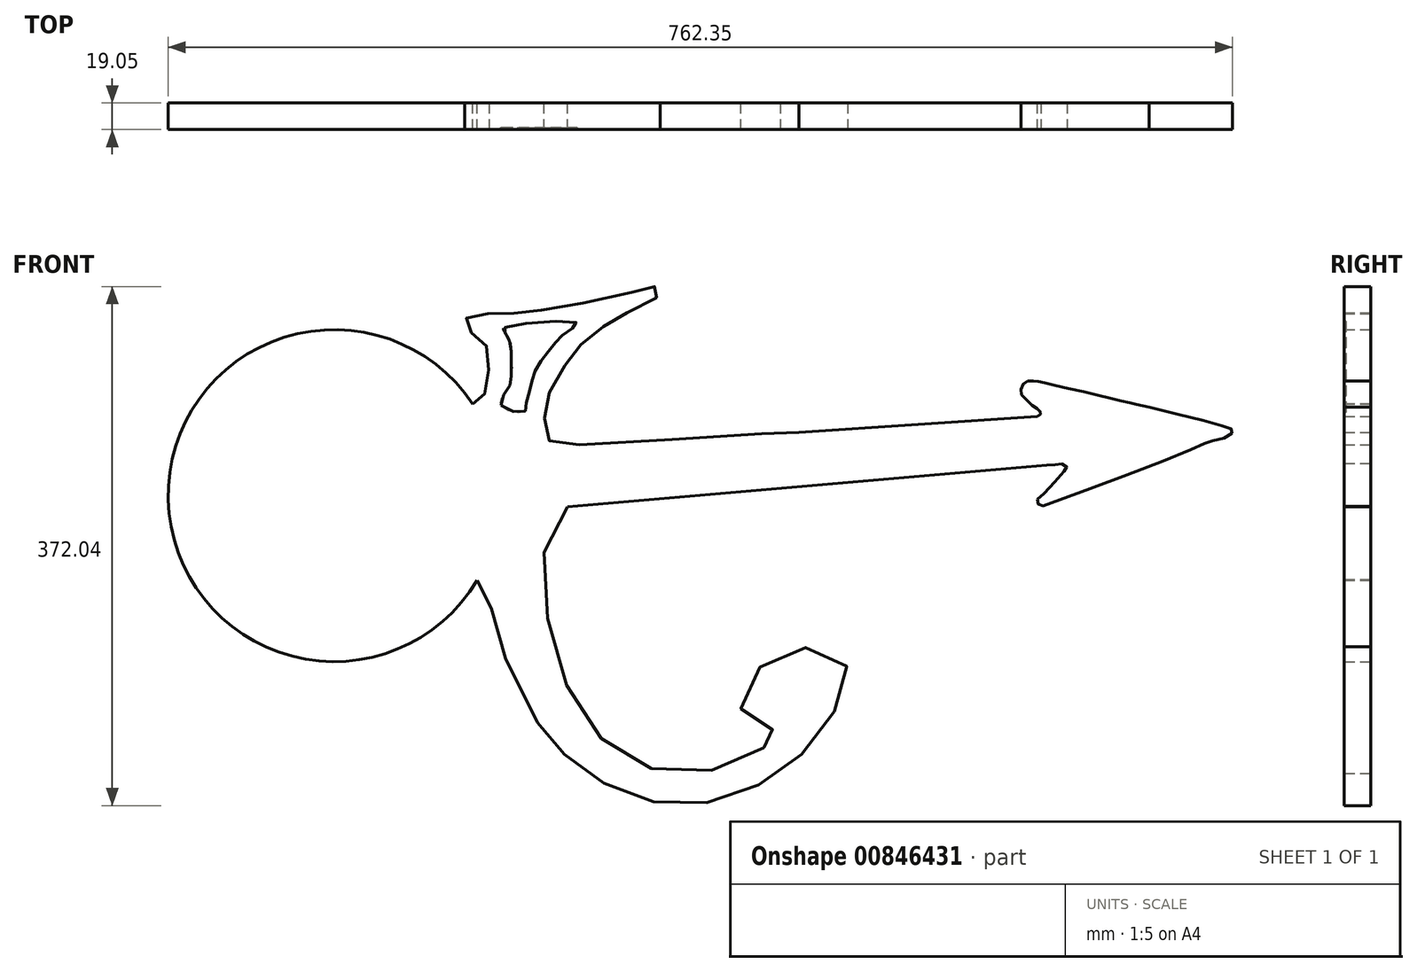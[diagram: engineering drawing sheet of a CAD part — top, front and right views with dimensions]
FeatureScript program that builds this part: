
annotation { "Feature Type Name" : "Feature", "Feature Type Description" : "" }
export const myFeature = defineFeature(function(context is Context, id is Id, definition is map)
    precondition{}
    {
        {
            var Q0;
            Q0=qCreatedBy(makeId("Front.planeOp"),FACE);
            var sketch = newSketch(context, id + "F0", { "sketchPlane" : qUnion([Q0])});
            skArc(sketch, "E0", {"start": v(-130.11, 85.53) * mm, "mid": v(-348.27, 16.89) * mm, "end": v(-127, -40.95) * mm});
            skFitSpline(sketch, "E1", {"points": [v(-130.11, 85.53) * mm, v(-127.54, 85.53) * mm, v(-123.05, 90.04) * mm, v(-119.7, 99.57) * mm, v(-118.57, 112.46) * mm, v(-119.41, 124.5) * mm, v(-123.05, 131.23) * mm, v(-130.11, 136) * mm, v(-134.82, 139.36) * mm, v(-135.38, 145.53) * mm, v(-130.11, 150) * mm, v(-118.29, 150.29) * mm, v(-104.56, 150.29) * mm, v(-90.55, 151.7) * mm, v(-71.5, 153.93) * mm, v(-25.54, 163.46) * mm, v(-2.84, 169.06) * mm, v(0, 169.62) * mm, v(3.6, 167.38) * mm, v(3.6, 164.02) * mm, v(-4.8, 158.14) * mm, v(-27.78, 146.93) * mm, v(-36.47, 141.04) * mm, v(-50.2, 130.4) * mm, v(-58.04, 121.15) * mm, v(-68.13, 107.42) * mm, v(-75.98, 91.16) * mm, v(-78.22, 78.55) * mm, v(-78.78, 65.95) * mm, v(-74.3, 58.1) * mm, v(-68.13, 56.14) * mm, v(74.22, 63.98) * mm, v(103.36, 65.1) * mm], "startDerivative": vector(181.45, -37.87) * mm, "endDerivative": vector(410.65, 5.44) * mm});
            skLineSegment(sketch, "E2", {"start": v(-62.29, 11.73) * mm, "end": v(280.92, 41.5) * mm});
            skLineSegment(sketch, "E3", {"start": v(103.36, 65.1) * mm, "end": v(274.42, 76.69) * mm});
            skFitSpline(sketch, "E4", {"points": [v(274.42, 76.69) * mm, v(276.7, 78.48) * mm, v(275.97, 80.66) * mm, v(270.52, 84.66) * mm, v(265.43, 89.75) * mm, v(262.7, 93.2) * mm, v(264.7, 100.47) * mm, v(271.25, 102.1) * mm, v(279.6, 100.65) * mm, v(323.94, 90.3) * mm, v(344.65, 85.39) * mm, v(354.18, 83.22) * mm], "startDerivative": vector(58.3, 31.52) * mm, "endDerivative": vector(96.9, -21.74) * mm});
            skFitSpline(sketch, "E5", {"points": [v(354.18, 83.22) * mm, v(411.37, 68.6) * mm, v(413.97, 66.88) * mm, v(412.24, 62.99) * mm, v(399.27, 59.1) * mm, v(388.04, 54.34) * mm, v(280.87, 13.29) * mm, v(275.68, 12.86) * mm, v(273.95, 16.31) * mm, v(277.4, 19.77) * mm, v(293.4, 37.06) * mm, v(295.56, 40.08) * mm, v(292.97, 42.24) * mm, v(288.65, 42.24) * mm, v(280.92, 41.5) * mm], "startDerivative": vector(481.46, -118.1) * mm, "endDerivative": vector(-146.74, -12.07) * mm});
            skFitSpline(sketch, "E6", {"points": [v(-127, -40.95) * mm, v(-121.29, -40.95) * mm, v(-118.6, -54.12) * mm, v(-113.25, -70.88) * mm, v(-106.54, -97.02) * mm, v(-86.43, -138.58) * mm, v(-75.7, -154.67) * mm, v(-66.32, -164.05) * mm, v(-51.58, -176.12) * mm, v(-32.8, -188.18) * mm, v(-11.36, -196.9) * mm, v(15.46, -202.26) * mm, v(38.25, -200.25) * mm, v(61.04, -193.54) * mm, v(87.85, -180.14) * mm, v(104.6, -166.73) * mm, v(121.37, -145.95) * mm, v(133.43, -127.18) * mm, v(138.8, -108.41) * mm, v(130.75, -92.33) * mm, v(109.3, -88.97) * mm, v(89.2, -94.34) * mm, v(70.42, -108.41) * mm, v(62.38, -126.51) * mm, v(63.72, -137.9) * mm, v(77.13, -146.62) * mm, v(87.85, -148.63) * mm, v(90.53, -151.31) * mm, v(85.17, -156.68) * mm, v(64.39, -168.07) * mm, v(36.9, -178.13) * mm, v(4.73, -177.46) * mm, v(-22.08, -166.73) * mm, v(-45.54, -145.95) * mm, v(-63.64, -114.45) * mm, v(-75.7, -73.56) * mm, v(-78.39, -40.95) * mm, v(-75.7, 0) * mm, v(-62.29, 11.73) * mm], "startDerivative": vector(493.19, 133.64) * mm, "endDerivative": vector(663.86, 344.27) * mm});
            skFitSpline(sketch, "E7", {"points": [v(-109.9, 84.64) * mm, v(-93.14, 79.95) * mm, v(-91.8, 85.3) * mm, v(-88.44, 98.05) * mm, v(-85.76, 108.77) * mm, v(-78.39, 120.17) * mm, v(-70.34, 130.22) * mm, v(-62.3, 137.6) * mm, v(-55.6, 143.63) * mm, v(-107.21, 140.28) * mm, v(-107.88, 138.26) * mm, v(-103.86, 130.9) * mm, v(-102.52, 118.83) * mm, v(-102.52, 104.08) * mm, v(-105.2, 96.03) * mm, v(-109.9, 84.64) * mm]});
            skSolve(sketch);
        }
        {
            var Q0;
            Q0=makeQuery(id+"F0.imprint","IMPRINT",FACE,{"disambiguationData":[TD([[makeQuery(id+"F0.imprint","IMPRINT",EDGE,{"derivedFrom":sQuery(id+"F0.wireOp",EDGE,"E0")}),1.0]])]});
            extrude(context, id + "F1", {"entities" : qUnion([Q0]), "depth" : 19.05 * mm, "offsetDistance" : 25.4 * mm});
        }
        {
            var Q0;
            Q0=makeQuery(id+"F0.imprint","IMPRINT",FACE,{"disambiguationData":[TD([[makeQuery(id+"F0.imprint","IMPRINT",EDGE,{"derivedFrom":sQuery(id+"F0.wireOp",EDGE,"E7")}),1.0]])]});
            extrude(context, id + "F2", {"entities" : qUnion([Q0]), "operationType" : NewBodyOperationType.ADD, "depth" : 17.78 * mm, "offsetDistance" : 25.4 * mm});
        }
    });
